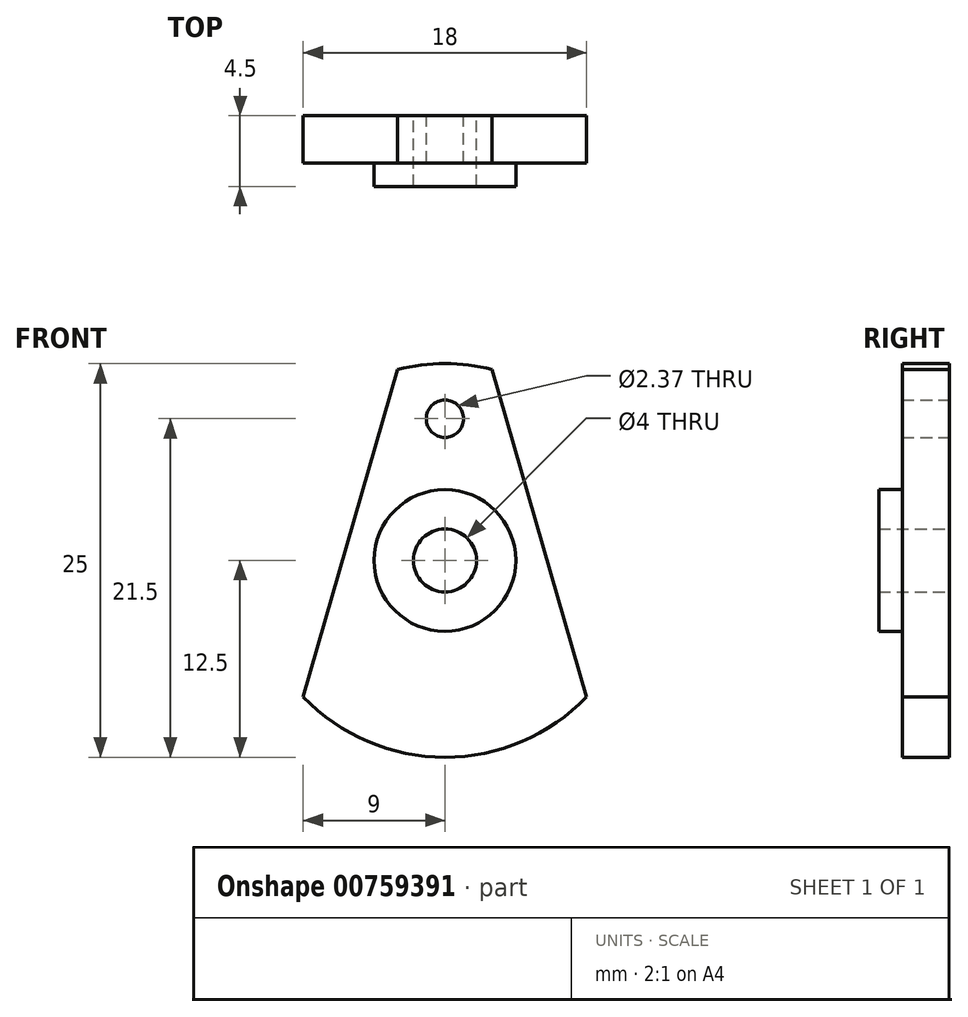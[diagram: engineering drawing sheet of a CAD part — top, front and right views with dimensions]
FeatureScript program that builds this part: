
annotation { "Feature Type Name" : "Feature", "Feature Type Description" : "" }
export const myFeature = defineFeature(function(context is Context, id is Id, definition is map)
    precondition{}
    {
        {
            var Q0;
            Q0=qCreatedBy(makeId("Front.planeOp"),FACE);
            var sketch = newSketch(context, id + "F0", { "sketchPlane" : qUnion([Q0])});
            skArc(sketch, "E0", {"start": v(-9, -8.67) * mm, "mid": v(0, -12.5) * mm, "end": v(9, -8.67) * mm});
            skCircle(sketch, "E1", {"center": v(0, 0) * mm, "radius": 4.5 * mm});
            skCircle(sketch, "E2", {"center": v(0, 0) * mm, "radius": 2 * mm});
            skLineSegment(sketch, "E3", {"start": v(3, 12.63) * mm, "end": v(3, 12.13) * mm, "construction": true});
            skLineSegment(sketch, "E4", {"start": v(9, -8.67) * mm, "end": v(9, -9.93) * mm, "construction": true});
            skLineSegment(sketch, "E5", {"start": v(3, 12.13) * mm, "end": v(9, -8.67) * mm});
            skLineSegment(sketch, "E6.MirrorCS", {"start": v(-3, 12.13) * mm, "end": v(-9, -8.67) * mm});
            skArc(sketch, "E7.trimOffspring", {"start": v(3, 12.13) * mm, "mid": v(0, 12.5) * mm, "end": v(-3, 12.13) * mm});
            skCircle(sketch, "E8", {"center": v(0, 9) * mm, "radius": 1.19 * mm});
            skSolve(sketch);
        }
        {
            var Q0;
            Q0=makeQuery(id+"F0.imprint","IMPRINT",FACE,{"disambiguationData":[TD([[makeQuery(id+"F0.imprint","IMPRINT",EDGE,{"derivedFrom":sQuery(id+"F0.wireOp",EDGE,"E1")}),1.0]])]});
            extrude(context, id + "F1", {"entities" : qUnion([Q0]), "depth" : 1.5 * mm, "offsetDistance" : 25 * mm});
        }
        {
            var Q0;
            Q0 = qSketchRegion(id + "F0", true);
            var Q1;
            Q1=makeQuery(id+"F1.opExtrude","CAP_FACE",FACE,{"disambiguationData":[OSD([sQuery(id+"F0.wireOp",EDGE,"E1"),sQuery(id+"F0.wireOp",EDGE,"E2")])],"isStart":false});
            extrude(context, id + "F2", {"entities" : qUnion([Q0, Q1]), "operationType" : NewBodyOperationType.ADD, "depth" : 3 * mm, "offsetDistance" : 25 * mm});
        }
    });
